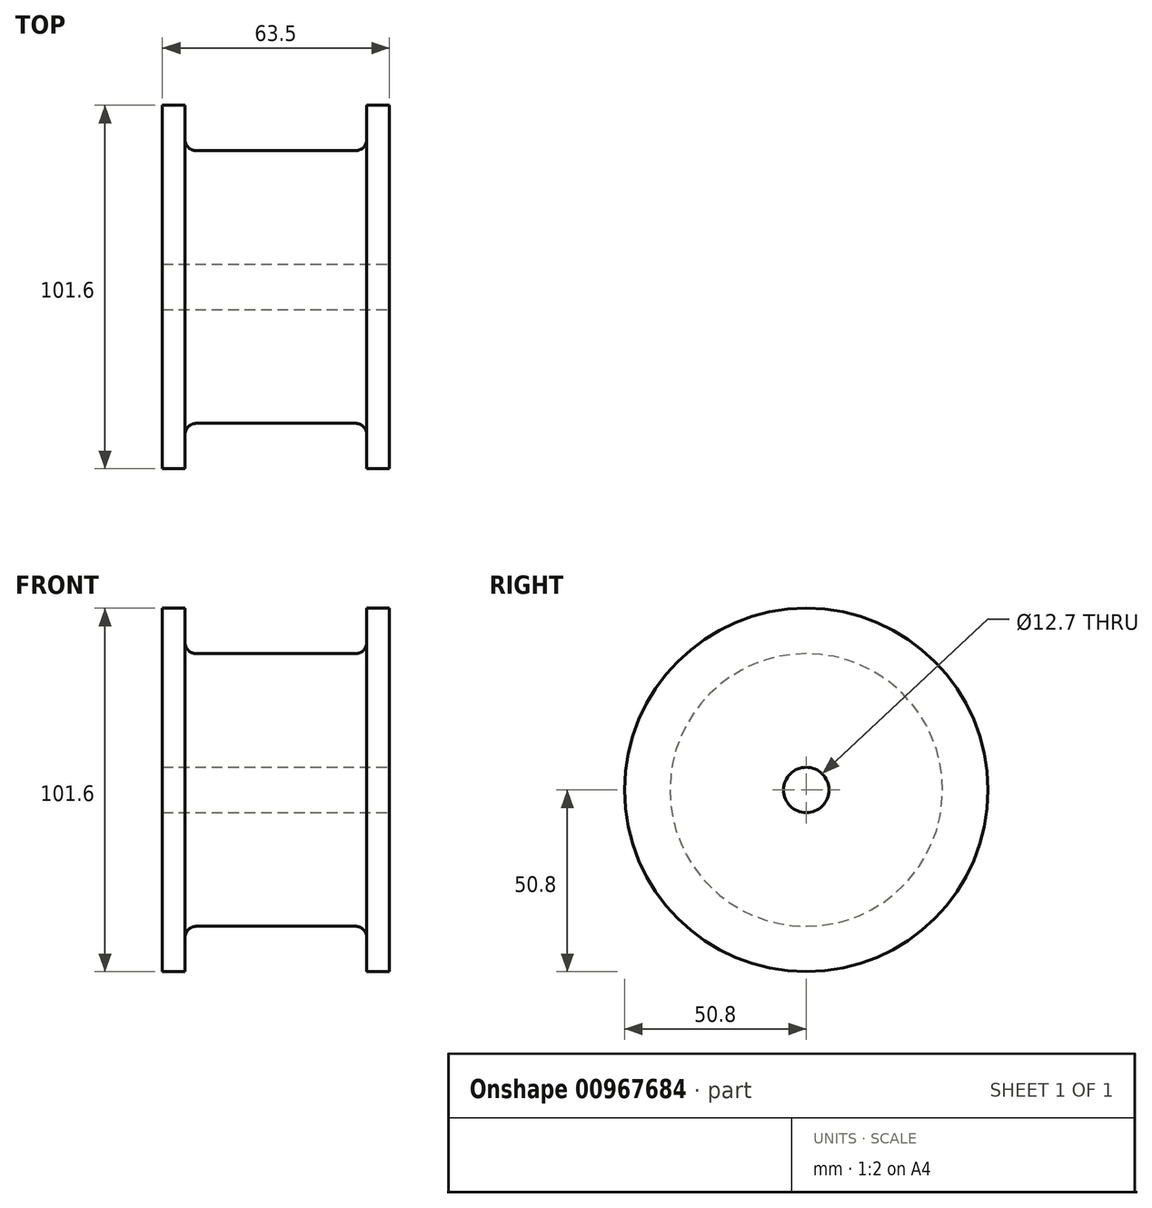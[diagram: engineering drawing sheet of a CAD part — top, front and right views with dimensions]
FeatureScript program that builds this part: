
annotation { "Feature Type Name" : "Feature", "Feature Type Description" : "" }
export const myFeature = defineFeature(function(context is Context, id is Id, definition is map)
    precondition{}
    {
        {
            var Q0;
            Q0=qCreatedBy(makeId("Right.planeOp"),FACE);
            var sketch = newSketch(context, id + "F0", { "sketchPlane" : qUnion([Q0])});
            skCircle(sketch, "E0", {"center": v(0, 0) * mm, "radius": 50.8 * mm});
            skSolve(sketch);
        }
        {
            var Q0;
            Q0 = qSketchRegion(id + "F0", true);
            extrude(context, id + "F1", {"entities" : qUnion([Q0]), "depth" : 63.5 * mm, "offsetDistance" : 25.4 * mm, "symmetric" : true});
        }
        {
            var Q0;
            Q0=qCreatedBy(makeId("Front.planeOp"),FACE);
            var sketch = newSketch(context, id + "F2", { "sketchPlane" : qUnion([Q0])});
            skLineSegment(sketch, "E1.bottom", {"start": v(22.22, 77.55) * mm, "end": v(-22.23, 77.55) * mm});
            skLineSegment(sketch, "E1.top", {"start": v(22.22, 38.1) * mm, "end": v(-22.23, 38.1) * mm});
            skLineSegment(sketch, "E1.left", {"start": v(25.4, 74.37) * mm, "end": v(25.4, 41.27) * mm});
            skLineSegment(sketch, "E1.right", {"start": v(-25.4, 74.37) * mm, "end": v(-25.4, 41.27) * mm});
            skPoint(sketch, "E1.middle", {"position": v(0, 57.82) * mm});
            skPoint(sketch, "E2.visualSharp", {"position": v(-25.4, 38.1) * mm});
            skArc(sketch, "E2.filletArc", {"start": v(-25.4, 41.27) * mm, "mid": v(-24.47, 39.03) * mm, "end": v(-22.23, 38.1) * mm});
            skPoint(sketch, "E3.visualSharp", {"position": v(25.4, 38.1) * mm});
            skArc(sketch, "E3.filletArc", {"start": v(22.22, 38.1) * mm, "mid": v(24.47, 39.03) * mm, "end": v(25.4, 41.27) * mm});
            skPoint(sketch, "E4.visualSharp", {"position": v(-25.4, 77.55) * mm});
            skArc(sketch, "E4.filletArc", {"start": v(-22.23, 77.55) * mm, "mid": v(-24.47, 76.62) * mm, "end": v(-25.4, 74.37) * mm});
            skPoint(sketch, "E5.visualSharp", {"position": v(25.4, 77.55) * mm});
            skArc(sketch, "E5.filletArc", {"start": v(25.4, 74.37) * mm, "mid": v(24.47, 76.62) * mm, "end": v(22.22, 77.55) * mm});
            skSolve(sketch);
        }
        {
            var Q0;
            Q0 = qSketchRegion(id + "F2", true);
            var Q1;
            Q1=makeQuery(id+"F1.opExtrude","SWEPT_FACE",FACE,{"disambiguationData":[OSD([sQuery(id+"F0.wireOp",EDGE,"E0")])]});
            revolve(context, id + "F3", {"operationType" : NewBodyOperationType.REMOVE, "surfaceOperationType" : NewSurfaceOperationType.NEW, "entities" : qUnion([Q0]), "axis" : qUnion([Q1]), "revolveType" : RevolveType.FULL, "oppositeDirection" : true});
        }
        {
            var Q0;
            Q0=qCreatedBy(makeId("Right.planeOp"),FACE);
            var sketch = newSketch(context, id + "F4", { "sketchPlane" : qUnion([Q0])});
            skCircle(sketch, "E6", {"center": v(0, 0) * mm, "radius": 6.35 * mm});
            skSolve(sketch);
        }
        {
            var Q0;
            Q0 = qSketchRegion(id + "F4", true);
            extrude(context, id + "F5", {"entities" : qUnion([Q0]), "operationType" : NewBodyOperationType.REMOVE, "endBound" : BoundingType.THROUGH_ALL, "oppositeDirection" : true, "depth" : 25.4 * mm, "offsetDistance" : 25.4 * mm, "hasSecondDirection" : true, "secondDirectionBound" : BoundingType.THROUGH_ALL, "secondDirectionOppositeDirection" : false, "secondDirectionDepth" : 25.4 * mm});
        }
    });
